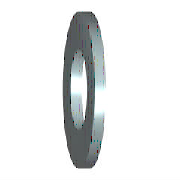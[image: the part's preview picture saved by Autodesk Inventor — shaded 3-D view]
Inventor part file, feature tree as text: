
AUTODESK INVENTOR PART (.ipt)
format: ipt  version: 2018 (Build 220112000, 112)  size: 109,056 bytes
history: native  units: mm (DEFAULTED — no unit token found)
features: extrude x1, other x1, plane x1, sketch x1
ambient origin geometry x7: Origin, YZ Plane, XY Plane, X Axis, Y Axis, Z Axis, Center Point
bodies: Solid1 (feature_tree)
feature tree (4):
  extrude  "Corpo"  Depth=21.4mm
  other  "Work Axis1"
  plane  "Work Plane1"
  sketch  "Schizzo"
